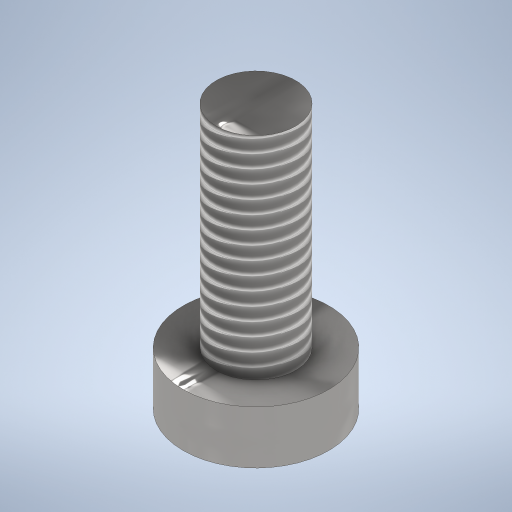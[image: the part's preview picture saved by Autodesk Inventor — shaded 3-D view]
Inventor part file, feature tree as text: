
AUTODESK INVENTOR PART (.ipt)
format: ipt  version: 2024.2 (Build 282272000, 272)  size: 317,440 bytes
history: native  units: mm
features: sketch x2, revolve x1, thread x1, extrude x1
ambient origin geometry x8: Origin, YZ Plane, XZ Plane, XY Plane, X Axis, Y Axis, Z Axis, Center Point
bodies: Solid1 (feature_tree)
feature tree (5):
  revolve  "Revolution1"  [1 undecoded]
  thread  "Thread1"  [1 undecoded]
  extrude  "Extrusion1"  [1 undecoded]
  sketch  "Sketch1"  dims[d4=90.0deg d5=6.0mm d6=0.0mm d0=0.0mm]
  sketch  "Sketch2"
note: 3 required parameter values undecoded (feature->parameter linkage not recoverable at this tier; creation-order binding heuristic only, values carry confidence <= 0.55)